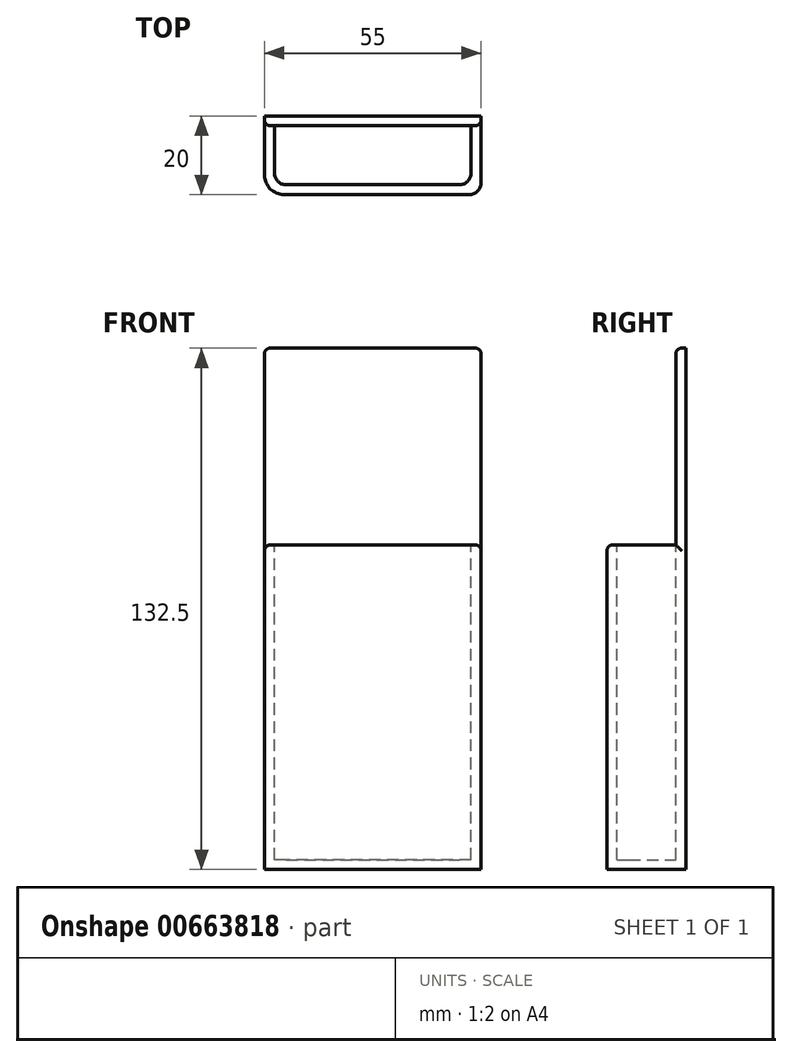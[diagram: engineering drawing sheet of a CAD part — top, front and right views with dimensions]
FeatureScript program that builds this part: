
annotation { "Feature Type Name" : "Feature", "Feature Type Description" : "" }
export const myFeature = defineFeature(function(context is Context, id is Id, definition is map)
    precondition{}
    {
        {
            var Q0;
            Q0=qCreatedBy(makeId("Top.planeOp"),FACE);
            var sketch = newSketch(context, id + "F0", { "sketchPlane" : qUnion([Q0])});
            skLineSegment(sketch, "E0.bottom", {"start": v(0, 0) * mm, "end": v(55, 0) * mm});
            skLineSegment(sketch, "E0.top", {"start": v(0, -20) * mm, "end": v(55, -20) * mm});
            skLineSegment(sketch, "E0.left", {"start": v(0, 0) * mm, "end": v(0, -20) * mm});
            skLineSegment(sketch, "E0.right", {"start": v(55, 0) * mm, "end": v(55, -20) * mm});
            skLineSegment(sketch, "E1.top", {"start": v(2.5, -17.5) * mm, "end": v(52.5, -17.5) * mm});
            skLineSegment(sketch, "E1.right", {"start": v(52.5, -2.5) * mm, "end": v(52.5, -17.5) * mm});
            skLineSegment(sketch, "E2", {"start": v(52.5, -2.5) * mm, "end": v(2.5, -2.5) * mm});
            skLineSegment(sketch, "E3", {"start": v(2.5, -17.5) * mm, "end": v(2.5, -2.5) * mm});
            skSolve(sketch);
        }
        {
            var Q0;
            Q0=makeQuery(id+"F0.imprint","IMPRINT",FACE,{"disambiguationData":[TD([[makeQuery(id+"F0.imprint","IMPRINT",EDGE,{"derivedFrom":sQuery(id+"F0.wireOp",EDGE,"E0.bottom")}),-1.0]])]});
            extrude(context, id + "F1", {"entities" : qUnion([Q0]), "oppositeDirection" : true, "depth" : 80 * mm, "offsetDistance" : 25 * mm});
        }
        {
            var Q0;
            Q0=qCreatedBy(makeId("Top.planeOp"),FACE);
            var sketch = newSketch(context, id + "F2", { "sketchPlane" : qUnion([Q0])});
            skLineSegment(sketch, "E4.bottom", {"start": v(0, 0) * mm, "end": v(55, 0) * mm});
            skLineSegment(sketch, "E4.top", {"start": v(0, -2.5) * mm, "end": v(55, -2.5) * mm});
            skLineSegment(sketch, "E4.left", {"start": v(0, 0) * mm, "end": v(0, -2.5) * mm});
            skLineSegment(sketch, "E4.right", {"start": v(55, 0) * mm, "end": v(55, -2.5) * mm});
            skSolve(sketch);
        }
        {
            var Q0;
            Q0 = qSketchRegion(id + "F2", true);
            extrude(context, id + "F3", {"entities" : qUnion([Q0]), "operationType" : NewBodyOperationType.ADD, "depth" : 50 * mm, "offsetDistance" : 25 * mm});
        }
        {
            var Q0;
            Q0=makeQuery(id+"F1.opExtrude","CAP_FACE",FACE,{"disambiguationData":[OSD([sQuery(id+"F0.wireOp",EDGE,"E0.bottom"),sQuery(id+"F0.wireOp",EDGE,"E0.top"),sQuery(id+"F0.wireOp",EDGE,"E0.left"),sQuery(id+"F0.wireOp",EDGE,"E0.right"),sQuery(id+"F0.wireOp",EDGE,"E1.top"),sQuery(id+"F0.wireOp",EDGE,"E1.right"),sQuery(id+"F0.wireOp",EDGE,"E2"),sQuery(id+"F0.wireOp",EDGE,"E3")])],"isStart":false});
            var sketch = newSketch(context, id + "F4", { "sketchPlane" : qUnion([Q0])});
            skLineSegment(sketch, "E5.bottom", {"start": v(0, 0) * mm, "end": v(55, 0) * mm});
            skLineSegment(sketch, "E5.top", {"start": v(0, 20) * mm, "end": v(55, 20) * mm});
            skLineSegment(sketch, "E5.left", {"start": v(0, 0) * mm, "end": v(0, 20) * mm});
            skLineSegment(sketch, "E5.right", {"start": v(55, 0) * mm, "end": v(55, 20) * mm});
            skSolve(sketch);
        }
        {
            var Q0;
            Q0 = qSketchRegion(id + "F4", true);
            extrude(context, id + "F5", {"entities" : qUnion([Q0]), "operationType" : NewBodyOperationType.ADD, "depth" : 2.5 * mm, "offsetDistance" : 25 * mm});
        }
        {
            var Q0;
            Q0=makeQuery(id+"F5.boolean.opBoolean","MERGE",EDGE,{"derivedFrom":[makeQuery(id+"F1.opExtrude","SWEPT_EDGE",EDGE,{"disambiguationData":[OSD([sQuery(id+"F0.wireOp",EDGE,"E0.top"),sQuery(id+"F0.wireOp",EDGE,"E0.left")])]}),makeQuery(id+"F5.opExtrude","SWEPT_EDGE",EDGE,{"disambiguationData":[OSD([sQuery(id+"F4.wireOp",EDGE,"E5.top"),sQuery(id+"F4.wireOp",EDGE,"E5.left")])]})]});
            fillet(context, id + "F6", {"entities" : qUnion([Q0]), "radius" : 5 * mm, "tangentPropagation" : true, "allowEdgeOverflow" : false});
        }
        {
            var Q0;
            Q0=makeQuery(id+"F1.opExtrude","SWEPT_EDGE",EDGE,{"disambiguationData":[OSD([sQuery(id+"F0.wireOp",EDGE,"E1.top"),sQuery(id+"F0.wireOp",EDGE,"E1.right")])]});
            var Q1;
            Q1=makeQuery(id+"F1.opExtrude","SWEPT_EDGE",EDGE,{"disambiguationData":[OSD([sQuery(id+"F0.wireOp",EDGE,"E1.top"),sQuery(id+"F0.wireOp",EDGE,"E3")])]});
            var Q2;
            Q2=makeQuery(id+"F5.boolean.opBoolean","MERGE",EDGE,{"derivedFrom":[makeQuery(id+"F1.opExtrude","SWEPT_EDGE",EDGE,{"disambiguationData":[OSD([sQuery(id+"F0.wireOp",EDGE,"E0.top"),sQuery(id+"F0.wireOp",EDGE,"E0.right")])]}),makeQuery(id+"F5.opExtrude","SWEPT_EDGE",EDGE,{"disambiguationData":[OSD([sQuery(id+"F4.wireOp",EDGE,"E5.top"),sQuery(id+"F4.wireOp",EDGE,"E5.right")])]})]});
            fillet(context, id + "F7", {"entities" : qUnion([Q0, Q1, Q2]), "radius" : 3 * mm, "tangentPropagation" : true, "allowEdgeOverflow" : false});
        }
        {
            var Q0;
            Q0=makeQuery(id+"F3.opExtrude","SWEPT_EDGE",EDGE,{"disambiguationData":[OSD([sQuery(id+"F2.wireOp",EDGE,"E4.top"),sQuery(id+"F2.wireOp",EDGE,"E4.right")])]});
            var Q1;
            Q1=makeQuery(id+"F3.opExtrude","SWEPT_EDGE",EDGE,{"disambiguationData":[OSD([sQuery(id+"F2.wireOp",EDGE,"E4.top"),sQuery(id+"F2.wireOp",EDGE,"E4.left")])]});
            fillet(context, id + "F8", {"entities" : qUnion([Q0, Q1]), "radius" : 1.5 * mm, "tangentPropagation" : true, "allowEdgeOverflow" : false});
        }
        {
            var Q0;
            Q0=makeQuery(id+"F3.opExtrude","CAP_EDGE",EDGE,{"disambiguationData":[OSD([sQuery(id+"F2.wireOp",EDGE,"E4.top")])],"isStart":false});
            var Q1;
            Q1=makeQuery(id+"F1.opExtrude","CAP_EDGE",EDGE,{"disambiguationData":[OSD([sQuery(id+"F0.wireOp",EDGE,"E0.left")])],"isStart":true});
            fillet(context, id + "F9", {"entities" : qUnion([Q0, Q1]), "radius" : 1.5 * mm, "tangentPropagation" : true, "allowEdgeOverflow" : false});
        }
    });
